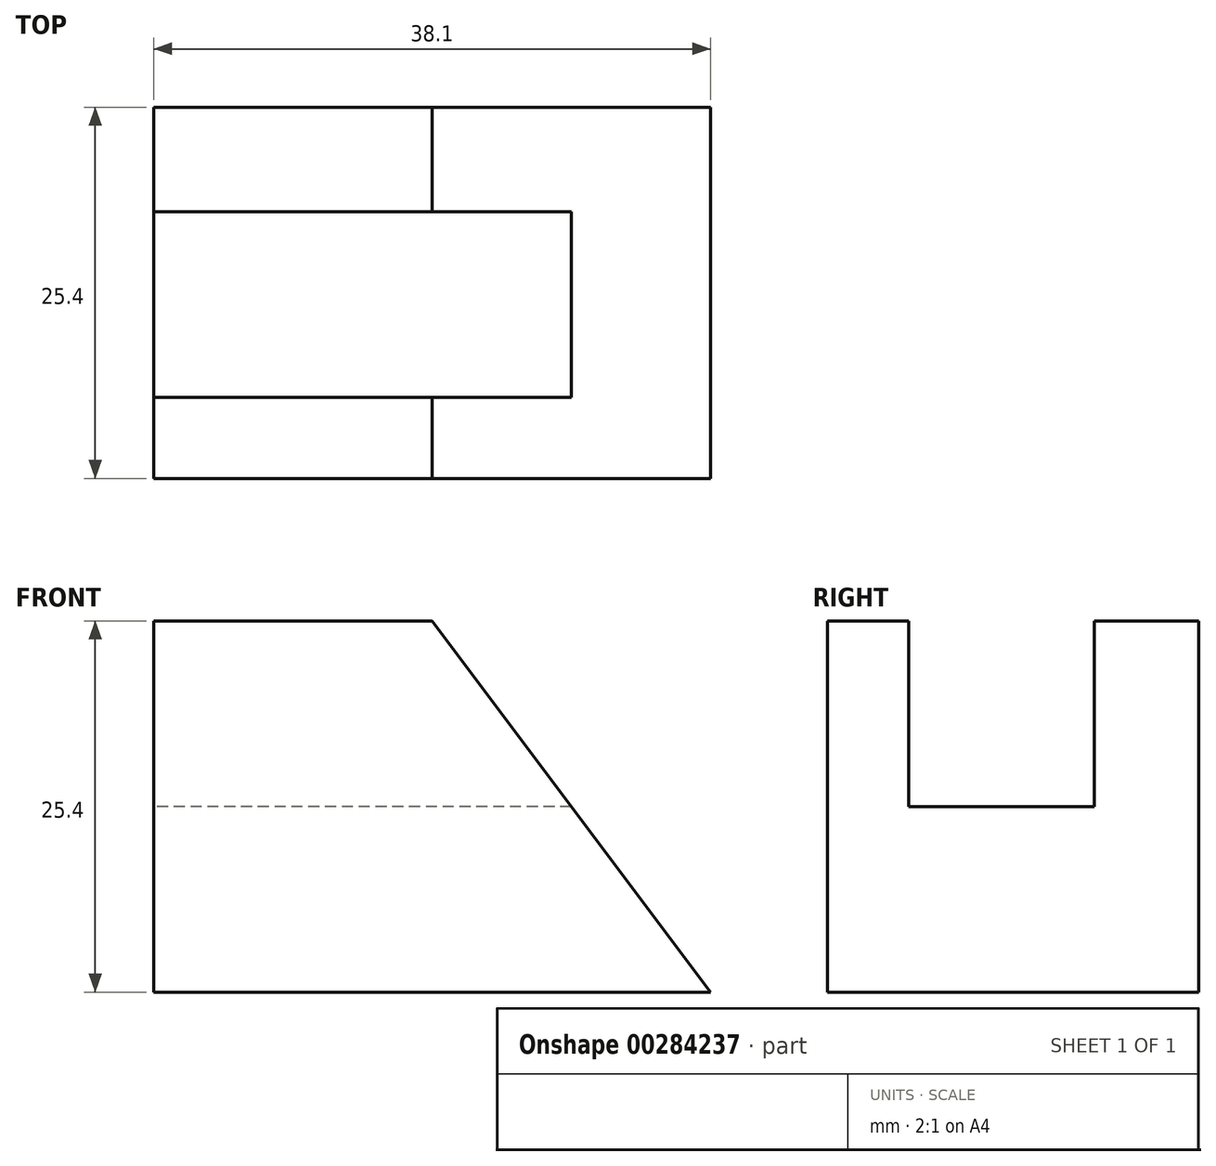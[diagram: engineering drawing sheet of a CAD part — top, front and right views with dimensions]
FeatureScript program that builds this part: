
annotation { "Feature Type Name" : "Feature", "Feature Type Description" : "" }
export const myFeature = defineFeature(function(context is Context, id is Id, definition is map)
    precondition{}
    {
        {
            var Q0;
            Q0=qCreatedBy(makeId("Front.planeOp"),FACE);
            var sketch = newSketch(context, id + "F0", { "sketchPlane" : qUnion([Q0])});
            skLineSegment(sketch, "E0", {"start": v(0, 0) * mm, "end": v(0, 25.4) * mm});
            skLineSegment(sketch, "E1", {"start": v(0, 25.4) * mm, "end": v(19.05, 25.4) * mm});
            skLineSegment(sketch, "E2", {"start": v(19.05, 25.4) * mm, "end": v(38.1, 0) * mm});
            skLineSegment(sketch, "E3", {"start": v(38.1, 0) * mm, "end": v(0, 0) * mm});
            skSolve(sketch);
        }
        {
            var Q0;
            Q0=makeQuery(id+"F0.imprint","IMPRINT",FACE,{"disambiguationData":[TD([[makeQuery(id+"F0.imprint","IMPRINT",EDGE,{"derivedFrom":sQuery(id+"F0.wireOp",EDGE,"E0")}),-1.0]])]});
            extrude(context, id + "F1", {"entities" : qUnion([Q0]), "endBound" : BoundingType.SYMMETRIC, "depth" : 25.4 * mm});
        }
        {
            var Q0;
            Q0=makeQuery(id+"F1.opExtrude","SWEPT_FACE",FACE,{"disambiguationData":[OSD([sQuery(id+"F0.wireOp",EDGE,"E0")])]});
            var sketch = newSketch(context, id + "F2", { "sketchPlane" : qUnion([Q0])});
            skLineSegment(sketch, "E4", {"start": v(-5.55, 25.4) * mm, "end": v(-5.55, 12.7) * mm});
            skLineSegment(sketch, "E5", {"start": v(-5.55, 12.7) * mm, "end": v(7.15, 12.7) * mm});
            skLineSegment(sketch, "E6", {"start": v(7.15, 12.7) * mm, "end": v(7.15, 25.4) * mm});
            skLineSegment(sketch, "E7", {"start": v(7.15, 25.4) * mm, "end": v(-5.55, 25.4) * mm});
            skSolve(sketch);
        }
        {
            var Q0;
            Q0=makeQuery(id+"F2.imprint","IMPRINT",FACE,{"disambiguationData":[TD([[makeQuery(id+"F2.imprint","IMPRINT",EDGE,{"derivedFrom":sQuery(id+"F2.wireOp",EDGE,"E4")}),1.0]])]});
            extrude(context, id + "F3", {"entities" : qUnion([Q0]), "operationType" : NewBodyOperationType.REMOVE, "endBound" : BoundingType.THROUGH_ALL, "oppositeDirection" : true, "depth" : 25.4 * mm});
        }
    });
